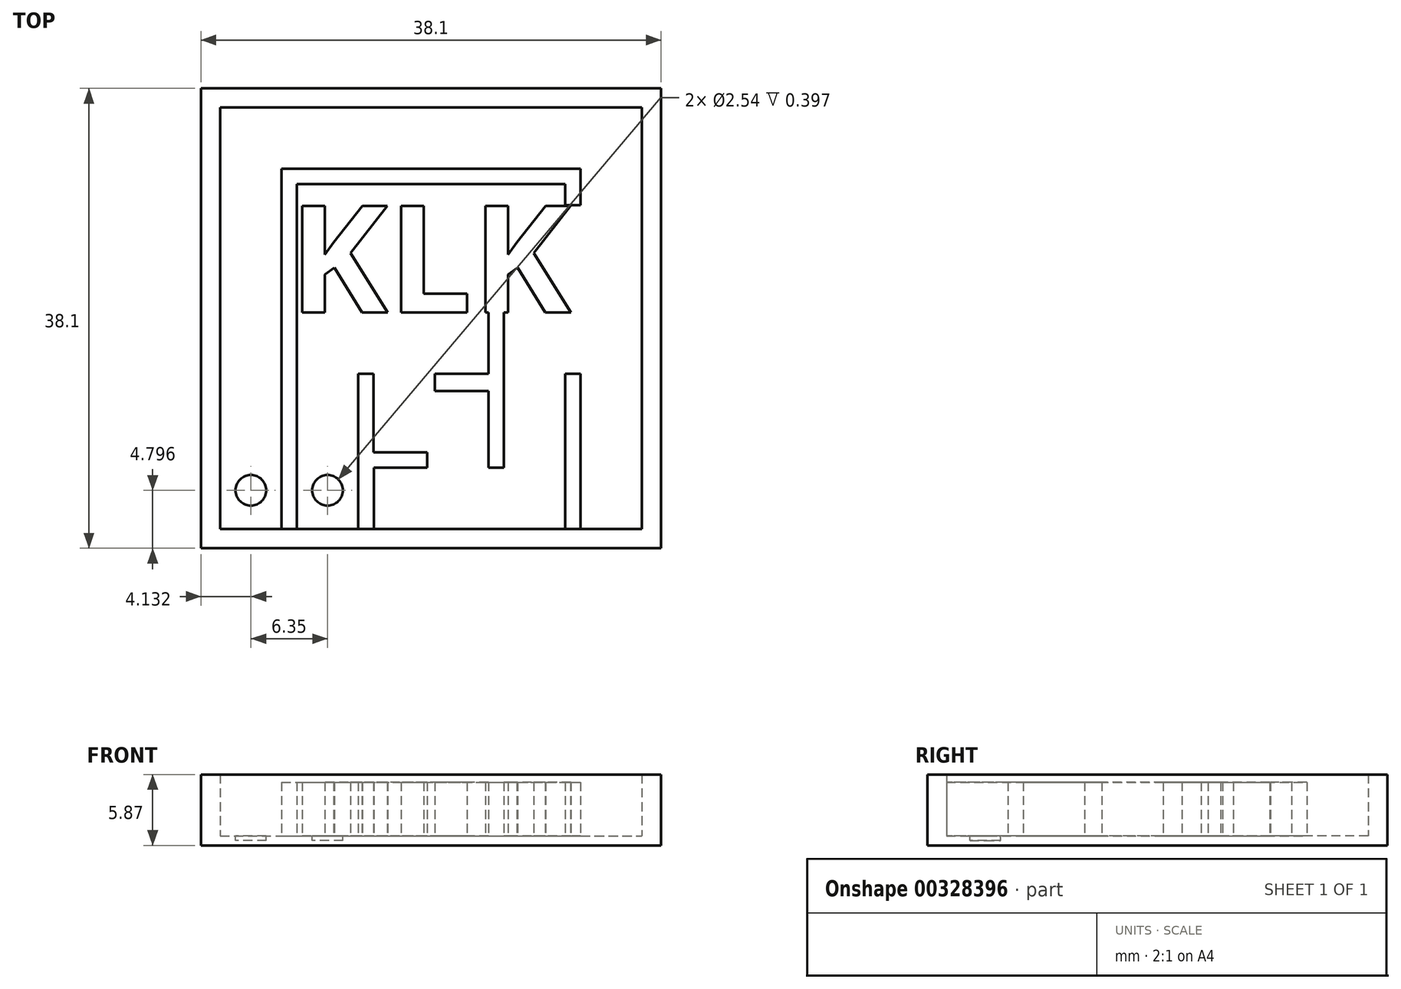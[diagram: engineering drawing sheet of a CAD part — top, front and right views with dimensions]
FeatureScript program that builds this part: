
annotation { "Feature Type Name" : "Feature", "Feature Type Description" : "" }
export const myFeature = defineFeature(function(context is Context, id is Id, definition is map)
    precondition{}
    {
        {
            var Q0;
            Q0=qCreatedBy(makeId("Top.planeOp"),FACE);
            var sketch = newSketch(context, id + "F0", { "sketchPlane" : qUnion([Q0])});
            skLineSegment(sketch, "E0.bottom", {"start": v(-15.87, 20.63) * mm, "end": v(22.23, 20.63) * mm});
            skLineSegment(sketch, "E0.top", {"start": v(-15.87, -17.47) * mm, "end": v(22.23, -17.47) * mm});
            skLineSegment(sketch, "E0.left", {"start": v(-15.87, 20.63) * mm, "end": v(-15.87, -17.47) * mm});
            skLineSegment(sketch, "E0.right", {"start": v(22.23, 20.63) * mm, "end": v(22.23, -17.47) * mm});
            skSolve(sketch);
        }
        {
            var Q0;
            Q0=makeQuery(id+"F0.imprint","IMPRINT",FACE,{"disambiguationData":[TD([[makeQuery(id+"F0.imprint","IMPRINT",EDGE,{"derivedFrom":sQuery(id+"F0.wireOp",EDGE,"E0.bottom")}),-1.0]])]});
            extrude(context, id + "F1", {"entities" : qUnion([Q0]), "depth" : 0.8 * mm});
        }
        {
            var Q0;
            Q0=makeQuery(id+"F1.opExtrude","CAP_FACE",FACE,{"disambiguationData":[OSD([sQuery(id+"F0.wireOp",EDGE,"E0.bottom"),sQuery(id+"F0.wireOp",EDGE,"E0.top"),sQuery(id+"F0.wireOp",EDGE,"E0.left"),sQuery(id+"F0.wireOp",EDGE,"E0.right")])],"isStart":false});
            var sketch = newSketch(context, id + "F2", { "sketchPlane" : qUnion([Q0])});
            skLineSegment(sketch, "E1.0", {"start": v(-14.28, 19.04) * mm, "end": v(20.65, 19.04) * mm});
            skLineSegment(sketch, "E1.1", {"start": v(-14.28, 19.04) * mm, "end": v(-14.28, -15.89) * mm});
            skLineSegment(sketch, "E1.2", {"start": v(-14.28, -15.89) * mm, "end": v(20.65, -15.89) * mm});
            skLineSegment(sketch, "E1.3", {"start": v(20.65, 19.04) * mm, "end": v(20.65, -15.89) * mm});
            skSolve(sketch);
        }
        {
            var Q0;
            Q0=makeQuery(id+"F2.imprint","IMPRINT",FACE,{"disambiguationData":[TD([[makeQuery(id+"F2.imprint","IMPRINT",EDGE,{"derivedFrom":sQuery(id+"F2.wireOp",EDGE,"E1.0")}),1.0]])]});
            extrude(context, id + "F3", {"entities" : qUnion([Q0]), "operationType" : NewBodyOperationType.ADD, "depth" : 5.08 * mm});
        }
        {
            var Q0;
            Q0=makeQuery(id+"F1.opExtrude","CAP_FACE",FACE,{"disambiguationData":[OSD([sQuery(id+"F0.wireOp",EDGE,"E0.bottom"),sQuery(id+"F0.wireOp",EDGE,"E0.top"),sQuery(id+"F0.wireOp",EDGE,"E0.left"),sQuery(id+"F0.wireOp",EDGE,"E0.right")])],"isStart":false});
            var sketch = newSketch(context, id + "F4", { "sketchPlane" : qUnion([Q0])});
            skLineSegment(sketch, "E2.bottom", {"start": v(-9.2, -15.89) * mm, "end": v(-7.93, -15.89) * mm});
            skLineSegment(sketch, "E2.top", {"start": v(-9.2, 13.96) * mm, "end": v(-7.93, 13.96) * mm});
            skLineSegment(sketch, "E2.left", {"start": v(-9.2, -15.89) * mm, "end": v(-9.2, 13.96) * mm});
            skLineSegment(sketch, "E2.right", {"start": v(-7.93, -15.89) * mm, "end": v(-7.93, 12.69) * mm});
            skLineSegment(sketch, "E3.left", {"start": v(-7.93, 10.54) * mm, "end": v(-7.93, 8.72) * mm});
            skLineSegment(sketch, "E4.bottom", {"start": v(15.57, 19.04) * mm, "end": v(16.9, 19.04) * mm});
            skText(sketch, "E5", { "text": "KLK", "fontName": "OpenSans-Bold.ttf"});
            skLineSegment(sketch, "E6.bottom", {"start": v(-7.93, 13.96) * mm, "end": v(15.57, 13.96) * mm});
            skLineSegment(sketch, "E6.top", {"start": v(-7.93, 12.69) * mm, "end": v(14.3, 12.69) * mm});
            skLineSegment(sketch, "E6.right", {"start": v(15.57, 13.96) * mm, "end": v(15.57, 12.69) * mm});
            skLineSegment(sketch, "E7.bottom", {"start": v(15.57, -3.02) * mm, "end": v(15.57, -3.02) * mm});
            skLineSegment(sketch, "E7.top", {"start": v(15.57, -10.8) * mm, "end": v(15.57, -10.8) * mm});
            skLineSegment(sketch, "E7.left", {"start": v(15.57, -3.02) * mm, "end": v(15.57, -10.8) * mm});
            skLineSegment(sketch, "E7.right", {"start": v(15.57, -3.02) * mm, "end": v(15.57, -10.8) * mm});
            skLineSegment(sketch, "E8.right", {"start": v(3.5, -3.02) * mm, "end": v(3.5, -4.46) * mm});
            skLineSegment(sketch, "E9.bottom", {"start": v(5.83, -4.46) * mm, "end": v(7.1, -4.46) * mm});
            skLineSegment(sketch, "E9.top", {"start": v(5.83, -3.02) * mm, "end": v(7.1, -3.02) * mm});
            skLineSegment(sketch, "E9.left", {"start": v(5.83, -3.02) * mm, "end": v(5.83, -3.02) * mm});
            skLineSegment(sketch, "E9.right", {"start": v(7.1, -3.02) * mm, "end": v(7.1, -3.02) * mm});
            skLineSegment(sketch, "E10.top", {"start": v(7.95, -10.8) * mm, "end": v(9.22, -10.8) * mm});
            skLineSegment(sketch, "E10.left", {"start": v(9.22, 2.09) * mm, "end": v(9.22, -4.35) * mm});
            skLineSegment(sketch, "E10.right", {"start": v(7.95, 2.09) * mm, "end": v(7.95, -3.02) * mm});
            skLineSegment(sketch, "E11.bottom", {"start": v(2.87, -9.54) * mm, "end": v(-1.58, -9.54) * mm});
            skLineSegment(sketch, "E11.top", {"start": v(2.87, -10.8) * mm, "end": v(-1.54, -10.8) * mm});
            skLineSegment(sketch, "E12.top", {"start": v(-1.58, -3.02) * mm, "end": v(-2.85, -3.02) * mm});
            skLineSegment(sketch, "E12.left", {"start": v(-1.58, -9.54) * mm, "end": v(-1.58, -3.02) * mm});
            skLineSegment(sketch, "E12.right", {"start": v(-2.85, -9.54) * mm, "end": v(-2.85, -3.02) * mm});
            skLineSegment(sketch, "E13", {"start": v(15.57, 12.69) * mm, "end": v(15.57, 10.95) * mm});
            skLineSegment(sketch, "E14", {"start": v(14.3, 12.69) * mm, "end": v(14.3, 10.95) * mm});
            skLineSegment(sketch, "E15", {"start": v(14.3, 10.95) * mm, "end": v(15.57, 10.95) * mm});
            skLineSegment(sketch, "E16.trimOffspring", {"start": v(7.95, -4.46) * mm, "end": v(7.1, -4.46) * mm});
            skLineSegment(sketch, "E17.trimOffspring", {"start": v(9.22, -4.35) * mm, "end": v(9.22, -10.8) * mm});
            skLineSegment(sketch, "E18.trimOffspring", {"start": v(7.95, -4.46) * mm, "end": v(7.95, -10.8) * mm});
            skLineSegment(sketch, "E19.trimOffspring", {"start": v(7.95, -3.02) * mm, "end": v(7.1, -3.02) * mm});
            skLineSegment(sketch, "E20.trimOffspring", {"start": v(5.83, -4.46) * mm, "end": v(3.5, -4.46) * mm});
            skLineSegment(sketch, "E21", {"start": v(2.87, -9.54) * mm, "end": v(2.87, -10.8) * mm});
            skLineSegment(sketch, "E22", {"start": v(-2.85, -9.54) * mm, "end": v(-2.85, -10.8) * mm});
            skLineSegment(sketch, "E23.top", {"start": v(-2.85, -15.89) * mm, "end": v(-1.54, -15.89) * mm});
            skLineSegment(sketch, "E23.left", {"start": v(-2.85, -10.8) * mm, "end": v(-2.85, -15.89) * mm});
            skLineSegment(sketch, "E23.right", {"start": v(-1.54, -10.8) * mm, "end": v(-1.54, -15.89) * mm});
            skLineSegment(sketch, "E24.bottom", {"start": v(15.57, -3.02) * mm, "end": v(14.3, -3.02) * mm});
            skLineSegment(sketch, "E24.top", {"start": v(15.57, -15.89) * mm, "end": v(14.3, -15.89) * mm});
            skLineSegment(sketch, "E24.left", {"start": v(15.57, -3.02) * mm, "end": v(15.57, -15.89) * mm});
            skLineSegment(sketch, "E24.right", {"start": v(14.3, -3.02) * mm, "end": v(14.3, -15.89) * mm});
            skLineSegment(sketch, "E25.trimOffspring", {"start": v(5.83, -3.02) * mm, "end": v(3.5, -3.02) * mm});
            skLineSegment(sketch, "E26", {"start": v(-14.28, -15.89) * mm, "end": v(-9.2, -15.89) * mm});
            skCircle(sketch, "E27", {"center": v(-11.74, -12.67) * mm, "radius": 1.27 * mm});
            skPoint(sketch, "E27.centerSnap0", {"position": v(-11.74, -15.89) * mm});
            skLineSegment(sketch, "E28", {"start": v(-7.93, -15.89) * mm, "end": v(-2.85, -15.89) * mm});
            skCircle(sketch, "E29", {"center": v(-5.39, -12.67) * mm, "radius": 1.27 * mm});
            skPoint(sketch, "E29.centerSnap0", {"position": v(-5.39, -15.89) * mm});
            const initialGuessF4  = {"E5": [-0.0086, 0.00206, 1, 0, 0.00889]};
            skSetInitialGuess(sketch, initialGuessF4);
            skSolve(sketch);
        }
        {
            var Q0;
            Q0=makeQuery(id+"F4.imprint","IMPRINT",FACE,{"disambiguationData":[TD([[makeQuery(id+"F4.imprint","IMPRINT",EDGE,{"derivedFrom":sQuery(id+"F4.wireOp",EDGE,"E8.right")}),1.0]])]});
            var Q1;
            Q1=makeQuery(id+"F4.imprint","IMPRINT",FACE,{"disambiguationData":[TD([[makeQuery(id+"F4.imprint","IMPRINT",EDGE,{"derivedFrom":sQuery(id+"F4.wireOp",EDGE,"E5.sketch_text.stroke-19")}),-1.0]])]});
            var Q2;
            Q2=makeQuery(id+"F4.imprint","IMPRINT",FACE,{"disambiguationData":[TD([[makeQuery(id+"F4.imprint","IMPRINT",EDGE,{"derivedFrom":sQuery(id+"F4.wireOp",EDGE,"E5.sketch_text.stroke-13")}),-1.0]])]});
            var Q3;
            Q3=makeQuery(id+"F4.imprint","IMPRINT",FACE,{"disambiguationData":[TD([[makeQuery(id+"F4.imprint","IMPRINT",EDGE,{"derivedFrom":sQuery(id+"F4.wireOp",EDGE,"E5.sketch_text.stroke-0")}),-1.0]])]});
            var Q4;
            Q4=makeQuery(id+"F4.imprint","IMPRINT",FACE,{"disambiguationData":[TD([[makeQuery(id+"F4.imprint","IMPRINT",EDGE,{"derivedFrom":sQuery(id+"F4.wireOp",EDGE,"E11.bottom")}),1.0]])]});
            var Q5;
            {var subQ3=sQuery(id+"F4.wireOp",EDGE,"E24.bottom");Q5=makeQuery(id+"F4.imprint","IMPRINT",FACE,{"disambiguationData":[TD([[makeQuery(id+"F4.imprint","IMPRINT",EDGE,{"derivedFrom":subQ3}),1.0]])]});}
            var Q6;
            {var subQ3=sQuery(id+"F4.wireOp",EDGE,"E2.bottom");Q6=makeQuery(id+"F4.imprint","IMPRINT",FACE,{"disambiguationData":[TD([[makeQuery(id+"F4.imprint","IMPRINT",EDGE,{"derivedFrom":subQ3}),1.0]])]});}
            extrude(context, id + "F5", {"entities" : qUnion([Q0, Q1, Q2, Q3, Q4, Q5, Q6]), "operationType" : NewBodyOperationType.ADD, "depth" : 4.44 * mm});
        }
        {
            var Q0;
            Q0=makeQuery(id+"F4.imprint","IMPRINT",FACE,{"disambiguationData":[TD([[makeQuery(id+"F4.imprint","IMPRINT",EDGE,{"derivedFrom":sQuery(id+"F4.wireOp",EDGE,"E27")}),1.0]])]});
            var Q1;
            Q1=makeQuery(id+"F4.imprint","IMPRINT",FACE,{"disambiguationData":[TD([[makeQuery(id+"F4.imprint","IMPRINT",EDGE,{"derivedFrom":sQuery(id+"F4.wireOp",EDGE,"E29")}),1.0]])]});
            extrude(context, id + "F6", {"entities" : qUnion([Q0, Q1]), "operationType" : NewBodyOperationType.REMOVE, "oppositeDirection" : true, "depth" : 0.4 * mm});
        }
    });
